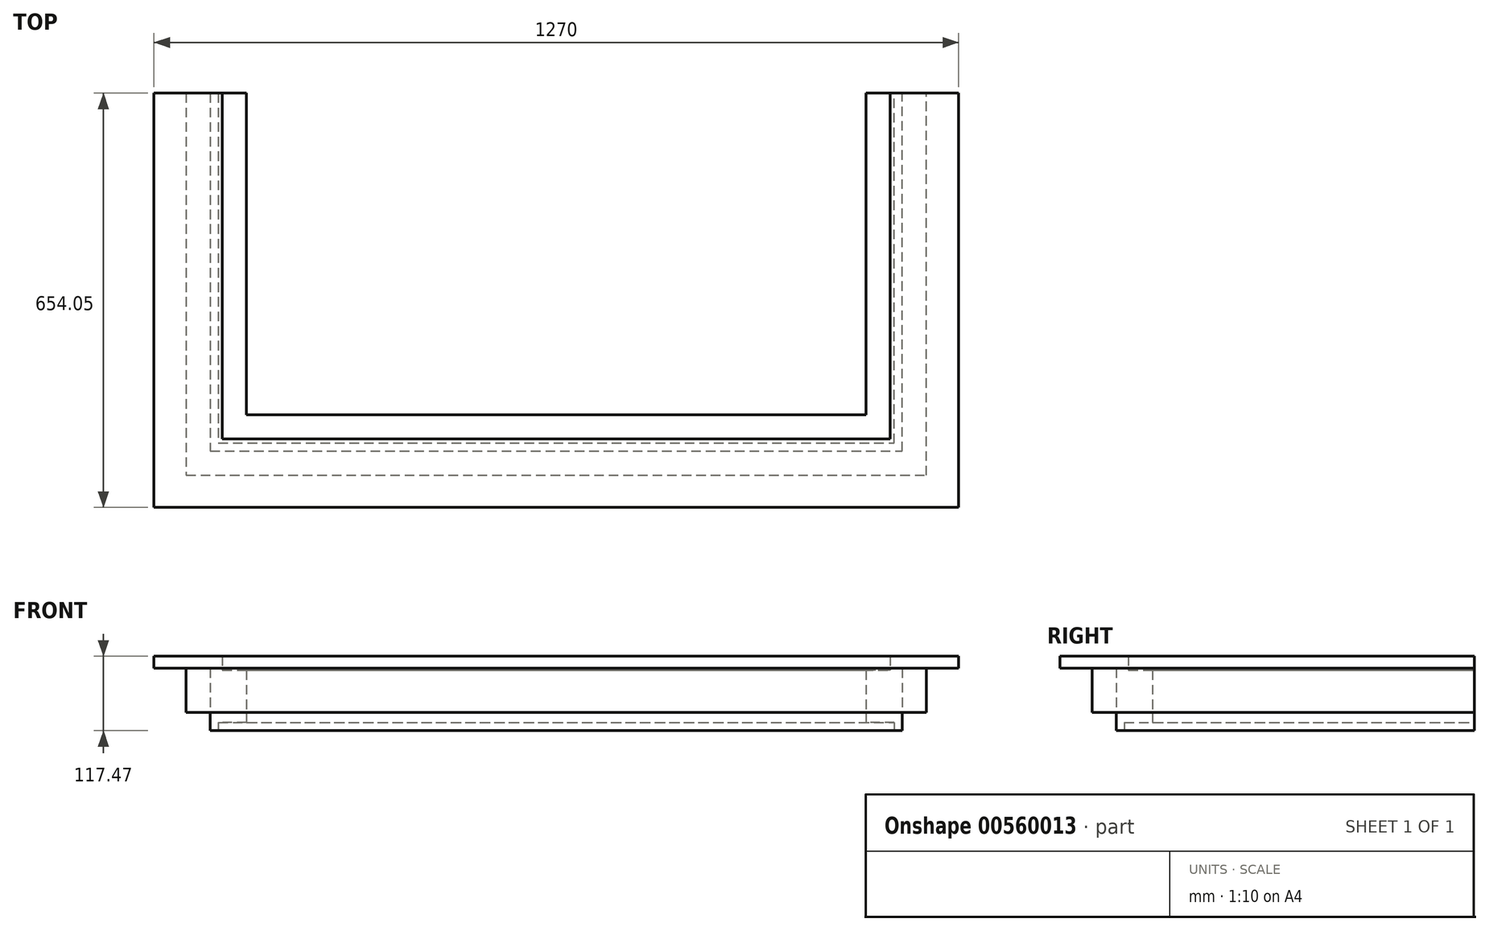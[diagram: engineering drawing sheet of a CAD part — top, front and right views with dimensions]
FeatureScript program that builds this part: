
annotation { "Feature Type Name" : "Feature", "Feature Type Description" : "" }
export const myFeature = defineFeature(function(context is Context, id is Id, definition is map)
    precondition{}
    {
        {
            var Q0;
            Q0=qCreatedBy(makeId("Top.planeOp"),FACE);
            var sketch = newSketch(context, id + "F0", { "sketchPlane" : qUnion([Q0])});
            skLineSegment(sketch, "E0.bottom", {"start": v(533.4, -279.4) * mm, "end": v(-533.4, -279.4) * mm});
            skLineSegment(sketch, "E0.top", {"start": v(533.4, 279.4) * mm, "end": v(-533.4, 279.4) * mm});
            skLineSegment(sketch, "E0.left", {"start": v(533.4, -279.4) * mm, "end": v(533.4, 279.4) * mm});
            skLineSegment(sketch, "E0.right", {"start": v(-533.4, -279.4) * mm, "end": v(-533.4, 279.4) * mm});
            skPoint(sketch, "E0.middle", {"position": v(0, 0) * mm});
            skSolve(sketch);
        }
        {
            var Q0;
            Q0=makeQuery(id+"F0.imprint","IMPRINT",FACE,{"disambiguationData":[TD([[makeQuery(id+"F0.imprint","IMPRINT",EDGE,{"derivedFrom":sQuery(id+"F0.wireOp",EDGE,"E0.bottom")}),-1.0]])]});
            var sketch = newSketch(context, id + "F1", { "sketchPlane" : qUnion([Q0])});
            skLineSegment(sketch, "E1.0", {"start": v(527.05, -273.05) * mm, "end": v(527.05, 273.05) * mm});
            skLineSegment(sketch, "E1.1", {"start": v(-527.05, -273.05) * mm, "end": v(527.05, -273.05) * mm});
            skLineSegment(sketch, "E1.2", {"start": v(-527.05, 273.05) * mm, "end": v(-527.05, -273.05) * mm});
            skLineSegment(sketch, "E1.3", {"start": v(527.05, 273.05) * mm, "end": v(488.95, 273.05) * mm});
            skLineSegment(sketch, "E2.1", {"start": v(488.95, -234.95) * mm, "end": v(488.95, 234.95) * mm});
            skLineSegment(sketch, "E2.2", {"start": v(-488.95, -234.95) * mm, "end": v(488.95, -234.95) * mm});
            skLineSegment(sketch, "E2.3", {"start": v(-488.95, 234.95) * mm, "end": v(-488.95, -234.95) * mm});
            skLineSegment(sketch, "E3", {"start": v(-488.95, 234.95) * mm, "end": v(-488.95, 273.05) * mm});
            skLineSegment(sketch, "E4", {"start": v(488.95, 234.95) * mm, "end": v(488.95, 273.05) * mm});
            skLineSegment(sketch, "E5.trimOffspring", {"start": v(-488.95, 273.05) * mm, "end": v(-527.05, 273.05) * mm});
            skSolve(sketch);
        }
        {
            var Q0;
            Q0=makeQuery(id+"F1.imprint","IMPRINT",FACE,{"disambiguationData":[TD([[makeQuery(id+"F1.imprint","IMPRINT",EDGE,{"derivedFrom":sQuery(id+"F1.wireOp",EDGE,"E1.0")}),1.0]])]});
            extrude(context, id + "F2", {"entities" : qUnion([Q0]), "depth" : 82.55 * mm, "offsetDistance" : 25.4 * mm});
        }
        {
            var Q0;
            Q0=qCreatedBy(makeId("Top.planeOp"),FACE);
            var sketch = newSketch(context, id + "F3", { "sketchPlane" : qUnion([Q0])});
            skLineSegment(sketch, "E6.0", {"start": v(-527.05, 273.05) * mm, "end": v(-527.05, -273.05) * mm});
            skLineSegment(sketch, "E7.0", {"start": v(527.05, -273.05) * mm, "end": v(527.05, 273.05) * mm});
            skLineSegment(sketch, "E8.0", {"start": v(-527.05, -273.05) * mm, "end": v(527.05, -273.05) * mm});
            skLineSegment(sketch, "E9.1", {"start": v(546.1, -292.1) * mm, "end": v(546.1, 273.05) * mm});
            skLineSegment(sketch, "E9.2", {"start": v(-546.1, -292.1) * mm, "end": v(546.1, -292.1) * mm});
            skLineSegment(sketch, "E9.3", {"start": v(-546.1, 273.05) * mm, "end": v(-546.1, -292.1) * mm});
            skLineSegment(sketch, "E10", {"start": v(-527.05, 273.05) * mm, "end": v(-546.1, 273.05) * mm});
            skLineSegment(sketch, "E11", {"start": v(527.05, 273.05) * mm, "end": v(546.1, 273.05) * mm});
            skSolve(sketch);
        }
        {
            var Q0;
            Q0=makeQuery(id+"F3.imprint","IMPRINT",FACE,{"disambiguationData":[TD([[makeQuery(id+"F3.imprint","IMPRINT",EDGE,{"derivedFrom":sQuery(id+"F3.wireOp",EDGE,"E6.0")}),-1.0]])]});
            extrude(context, id + "F4", {"entities" : qUnion([Q0]), "depth" : 85.72 * mm, "offsetDistance" : 25.4 * mm});
        }
        {
            var Q0;
            Q0=makeQuery(id+"F4.opExtrude","CAP_FACE",FACE,{"disambiguationData":[OSD([sQuery(id+"F3.wireOp",EDGE,"E6.0"),sQuery(id+"F3.wireOp",EDGE,"ce402062-60ec-4c50-a134-d0ef9bae9cc8.0"),sQuery(id+"F3.wireOp",EDGE,"E7.0"),sQuery(id+"F3.wireOp",EDGE,"E8.0"),sQuery(id+"F3.wireOp",EDGE,"E9.0"),sQuery(id+"F3.wireOp",EDGE,"E9.1"),sQuery(id+"F3.wireOp",EDGE,"E9.2"),sQuery(id+"F3.wireOp",EDGE,"E9.3")])],"isStart":true});
            extrude(context, id + "F5", {"entities" : qUnion([Q0]), "operationType" : NewBodyOperationType.ADD, "depth" : 12.7 * mm, "offsetDistance" : 25.4 * mm});
        }
        {
            var Q0;
            Q0=makeQuery(id+"F5.opExtrude","CAP_FACE",FACE,{"disambiguationData":[OSD([sQuery(id+"F3.wireOp",EDGE,"E6.0"),sQuery(id+"F3.wireOp",EDGE,"ce402062-60ec-4c50-a134-d0ef9bae9cc8.0"),sQuery(id+"F3.wireOp",EDGE,"E7.0"),sQuery(id+"F3.wireOp",EDGE,"E8.0"),sQuery(id+"F3.wireOp",EDGE,"E9.0"),sQuery(id+"F3.wireOp",EDGE,"E9.1"),sQuery(id+"F3.wireOp",EDGE,"E9.2"),sQuery(id+"F3.wireOp",EDGE,"E9.3")])],"isStart":false});
            var sketch = newSketch(context, id + "F6", { "sketchPlane" : qUnion([Q0])});
            skLineSegment(sketch, "E12.0", {"start": v(533.4, 279.4) * mm, "end": v(533.4, -273.05) * mm});
            skLineSegment(sketch, "E12.1", {"start": v(-533.4, 279.4) * mm, "end": v(533.4, 279.4) * mm});
            skLineSegment(sketch, "E12.2", {"start": v(-533.4, -273.05) * mm, "end": v(-533.4, 279.4) * mm});
            skSolve(sketch);
        }
        {
            var Q0;
            {var subQ2=sQuery(id+"F6.wireOp",EDGE,"E12.0");Q0=makeQuery(id+"F6.imprint","IMPRINT",FACE,{"disambiguationData":[TD([[makeQuery(id+"F6.imprint","IMPRINT",EDGE,{"derivedFrom":subQ2}),-1.0]])]});}
            extrude(context, id + "F7", {"entities" : qUnion([Q0]), "operationType" : NewBodyOperationType.REMOVE, "oppositeDirection" : true, "depth" : 12.7 * mm, "offsetDistance" : 25.4 * mm});
        }
        {
            var Q0;
            Q0=makeQuery(id+"F4.opExtrude","CAP_FACE",FACE,{"disambiguationData":[OSD([sQuery(id+"F3.wireOp",EDGE,"E6.0"),sQuery(id+"F3.wireOp",EDGE,"E7.0"),sQuery(id+"F3.wireOp",EDGE,"E8.0"),sQuery(id+"F3.wireOp",EDGE,"E9.1"),sQuery(id+"F3.wireOp",EDGE,"E9.2"),sQuery(id+"F3.wireOp",EDGE,"E9.3"),sQuery(id+"F3.wireOp",EDGE,"E10"),sQuery(id+"F3.wireOp",EDGE,"E11")])],"isStart":false});
            var sketch = newSketch(context, id + "F8", { "sketchPlane" : qUnion([Q0])});
            skLineSegment(sketch, "E13.0", {"start": v(-546.1, 273.05) * mm, "end": v(-546.1, -292.1) * mm});
            skLineSegment(sketch, "E14.0", {"start": v(-546.1, -292.1) * mm, "end": v(546.1, -292.1) * mm});
            skLineSegment(sketch, "E15.0", {"start": v(546.1, -292.1) * mm, "end": v(546.1, 273.05) * mm});
            skLineSegment(sketch, "E16.0", {"start": v(584.2, -330.2) * mm, "end": v(584.2, 273.05) * mm});
            skLineSegment(sketch, "E16.1", {"start": v(-584.2, -330.2) * mm, "end": v(584.2, -330.2) * mm});
            skLineSegment(sketch, "E16.2", {"start": v(-584.2, 273.05) * mm, "end": v(-584.2, -330.2) * mm});
            skLineSegment(sketch, "E17", {"start": v(-584.2, 273.05) * mm, "end": v(-546.1, 273.05) * mm});
            skLineSegment(sketch, "E18", {"start": v(546.1, 273.05) * mm, "end": v(584.2, 273.05) * mm});
            skSolve(sketch);
        }
        {
            var Q0;
            Q0=makeQuery(id+"F8.imprint","IMPRINT",FACE,{"disambiguationData":[TD([[makeQuery(id+"F8.imprint","IMPRINT",EDGE,{"derivedFrom":sQuery(id+"F8.wireOp",EDGE,"E13.0")}),-1.0]])]});
            extrude(context, id + "F9", {"entities" : qUnion([Q0]), "oppositeDirection" : true, "depth" : 69.85 * mm, "offsetDistance" : 25.4 * mm});
        }
        {
            var Q0;
            Q0=makeQuery(id+"F9.opExtrude","CAP_FACE",FACE,{"disambiguationData":[OSD([sQuery(id+"F8.wireOp",EDGE,"E13.0"),sQuery(id+"F8.wireOp",EDGE,"E14.0"),sQuery(id+"F8.wireOp",EDGE,"E15.0"),sQuery(id+"F8.wireOp",EDGE,"E16.0"),sQuery(id+"F8.wireOp",EDGE,"E16.1"),sQuery(id+"F8.wireOp",EDGE,"E16.2"),sQuery(id+"F8.wireOp",EDGE,"E17"),sQuery(id+"F8.wireOp",EDGE,"E18")])],"isStart":true});
            var sketch = newSketch(context, id + "F10", { "sketchPlane" : qUnion([Q0])});
            skLineSegment(sketch, "E19.0", {"start": v(635, -381) * mm, "end": v(635, 273.05) * mm});
            skLineSegment(sketch, "E19.1", {"start": v(-635, -381) * mm, "end": v(635, -381) * mm});
            skLineSegment(sketch, "E19.2", {"start": v(-635, 273.05) * mm, "end": v(-635, -381) * mm});
            skLineSegment(sketch, "E20.0", {"start": v(527.05, -273.05) * mm, "end": v(527.05, 273.05) * mm});
            skLineSegment(sketch, "E20.1", {"start": v(-527.05, -273.05) * mm, "end": v(527.05, -273.05) * mm});
            skLineSegment(sketch, "E20.2", {"start": v(-527.05, 273.05) * mm, "end": v(-527.05, -273.05) * mm});
            skLineSegment(sketch, "E21", {"start": v(-635, 273.05) * mm, "end": v(-527.05, 273.05) * mm});
            skLineSegment(sketch, "E22", {"start": v(527.05, 273.05) * mm, "end": v(635, 273.05) * mm});
            skSolve(sketch);
        }
        {
            var Q0;
            Q0 = qSketchRegion(id + "F10", true);
            extrude(context, id + "F11", {"entities" : qUnion([Q0]), "depth" : 19.05 * mm, "offsetDistance" : 25.4 * mm});
        }
    });
